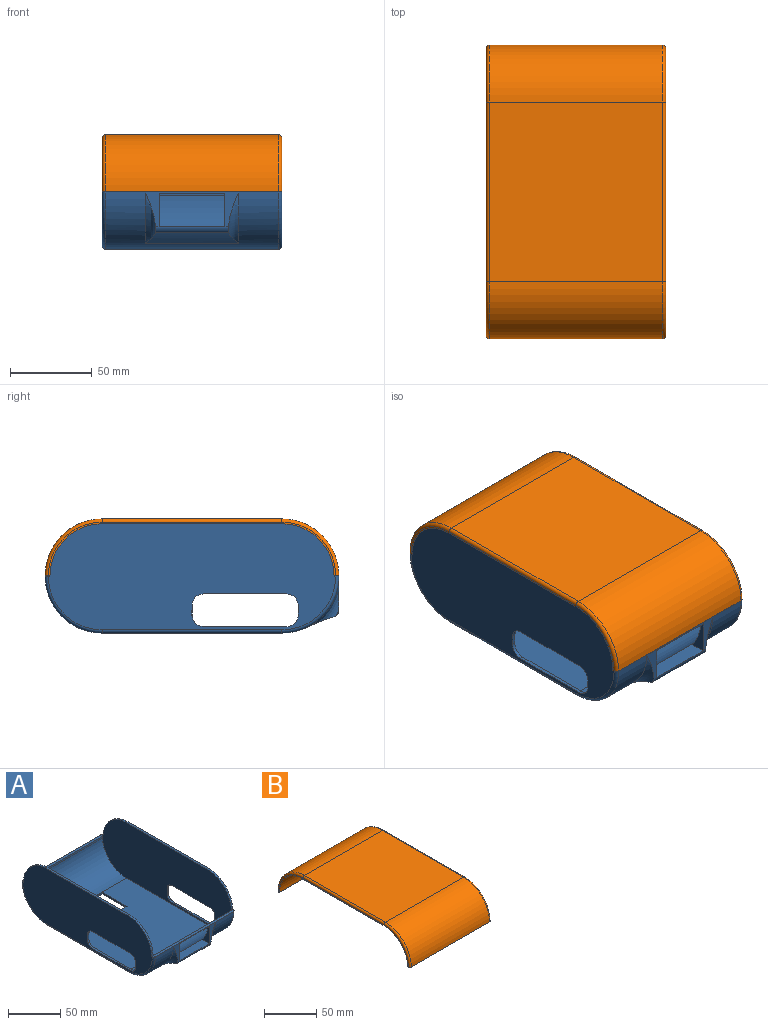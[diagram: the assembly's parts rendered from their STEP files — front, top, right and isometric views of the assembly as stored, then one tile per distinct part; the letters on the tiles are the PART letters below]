
ASSEMBLY  parts=2 mates=1
PART A: 307 faces, bbox 110x196.9x76 mm
  f0: plane 110x106mm, normal (0,0,-1), area 9197.1mm2, adj f6,f7,f38,f39,f40,f41,f42,f43
  f1: plane 110x106mm, normal (0,0,1), area 10332mm2, adj f17,f18,f20,f21,f38,f39,f40,f41
  f2: cylinder r=32mm len=32mm, axis (-1,0,0), area 100.5mm2, adj f4,f8,f13,f21
  f3: cylinder r=32mm len=32mm, axis (-1,0,0), area 100.5mm2, adj f4,f5,f13,f21
  f4: plane 110x2mm, normal (0,0,1), area 220mm2, adj f2,f3,f13,f21
  f5: plane 110x3mm, normal (0,0,1), area 328.3mm2, adj f3,f6,f11,f12,f13,f15,f291,f301
  f6: cylinder r=35mm len=106mm, axis (-1,0,0), area 3603.4mm2, adj f0,f5,f298,f299,f300,f301,f304
  f7: cylinder r=35mm len=106mm, axis (-1,0,0), area 5827.7mm2, adj f0,f8,f303,f306
  f8: plane 110x3mm, normal (0,0,1), area 328.3mm2, adj f2,f7,f9,f12,f13,f14,f303,f306
  f9: cylinder r=32mm len=32mm, axis (-1,0,0), area 100.5mm2, adj f8,f10,f12,f20
  f10: plane 110x2mm, normal (0,0,1), area 220mm2, adj f9,f11,f12,f20
  f11: cylinder r=32mm len=32mm, axis (-1,0,0), area 100.5mm2, adj f5,f10,f12,f20
  f12: plane 176x65mm, normal (1,0,0), area 9211.2mm2, adj f5,f8,f9,f10,f11,f22,f23,f24
  f13: plane 176x65mm, normal (-1,0,0), area 9211.2mm2, adj f2,f3,f4,f5,f8,f30,f31,f32
  f14: cylinder r=32mm len=106mm, axis (-1,0,0), area 212.1mm2, adj f8,f19,f20,f21
  f15: cylinder r=32mm len=106mm, axis (-1,0,0), area 212.1mm2, adj f5,f16,f20,f21
  f16: plane 106x1mm, normal (0,0,-1), area 106.2mm2, adj f15,f17,f20,f21,f292
  f17: cylinder r=33mm len=106mm, axis (-1,0,0), area 4437.5mm2, adj f1,f16,f20,f21,f294,f295,f296
  f18: cylinder r=33mm len=106mm, axis (-1,0,0), area 5282.5mm2, adj f1,f19,f20,f21
  f19: plane 106x1mm, normal (0,0,-1), area 106.2mm2, adj f14,f18,f20,f21
  f20: plane 175.88x65mm, normal (-1,0,0), area 9207.2mm2, adj f1,f9,f10,f11,f14,f15,f16,f17
  f21: plane 175.88x65mm, normal (1,0,0), area 9207.2mm2, adj f1,f2,f3,f4,f14,f15,f16,f17
  f22: plane 51x2mm, normal (0,0,-1), area 102mm2, adj f12,f20,f23,f29
  f23: cylinder r=7mm len=7mm, axis (1,0,0), area 22mm2, adj f12,f20,f22,f24
  f24: plane 6x2mm, normal (0,1,0), area 12mm2, adj f12,f20,f23,f25
  f25: cylinder r=7mm len=7mm, axis (1,0,0), area 22mm2, adj f12,f20,f24,f26
  f26: plane 51x2mm, normal (0,0,1), area 102mm2, adj f12,f20,f25,f27
  f27: cylinder r=7mm len=7mm, axis (1,0,0), area 22mm2, adj f12,f20,f26,f28
  f28: plane 6x2mm, normal (0,-1,0), area 12mm2, adj f12,f20,f27,f29
  f29: cylinder r=7mm len=7mm, axis (1,0,0), area 22mm2, adj f12,f20,f22,f28
  f30: plane 51x2mm, normal (0,0,-1), area 102mm2, adj f13,f21,f31,f37
  f31: cylinder r=7mm len=7mm, axis (-1,0,0), area 22mm2, adj f13,f21,f30,f32
  f32: plane 6x2mm, normal (0,-1,0), area 12mm2, adj f13,f21,f31,f33
  f33: cylinder r=7mm len=7mm, axis (-1,0,0), area 22mm2, adj f13,f21,f32,f34
  f34: plane 51x2mm, normal (0,0,1), area 102mm2, adj f13,f21,f33,f35
  f35: cylinder r=7mm len=7mm, axis (-1,0,0), area 22mm2, adj f13,f21,f34,f36
  f36: plane 6x2mm, normal (0,1,0), area 12mm2, adj f13,f21,f35,f37
  f37: cylinder r=7mm len=7mm, axis (-1,0,0), area 22mm2, adj f13,f21,f30,f36
  f38: plane 33.2x2mm, normal (-1,0,0), area 66.4mm2, adj f0,f1,f39,f41
  f39: plane 40x2mm, normal (0,1,0), area 80mm2, adj f0,f1,f38,f40
  f40: plane 33.2x2mm, normal (1,0,0), area 66.4mm2, adj f0,f1,f39,f41
  f41: plane 40x2mm, normal (0,-1,0), area 80mm2, adj f0,f1,f38,f40
  f42: plane 8.1x4.32mm, normal (0.88,0.47,0), area 9.2mm2, adj f0,f43,f50,f51
  f43: plane 8.1x4.29mm, normal (-0.88,0.47,0), area 9.2mm2, adj f0,f42,f44,f51
  f44: plane 2.06x1mm, normal (0,1,0), area 2.1mm2, adj f0,f43,f45,f51
  f45: plane 10.01x5.4mm, normal (0.88,-0.47,0), area 11.4mm2, adj f0,f44,f46,f51
  f46: plane 6.19x1mm, normal (1,0,0), area 6.2mm2, adj f0,f45,f47,f51
  f47: plane 1.9x1mm, normal (0,-1,0), area 1.9mm2, adj f0,f46,f48,f51
  f48: plane 6.28x1mm, normal (-1,0,0), area 6.3mm2, adj f0,f47,f49,f51
  f49: plane 9.92x5.41mm, normal (-0.88,-0.48,0), area 11.3mm2, adj f0,f48,f50,f51
  f50: plane 2.04x1mm, normal (0,1,0), area 2mm2, adj f0,f42,f49,f51
  f51: plane 16.2x12.71mm, normal (0,0,-1), area 49.8mm2, adj f42,f43,f44,f45,f46,f47,f48,f49
  f52: extruded ~1x0.94mm, area 0.9mm2, adj f0,f53,f70,f71
  f53: extruded ~1.43x1mm, area 1.6mm2, adj f0,f52,f54,f71
  f54: extruded ~1.68x1mm, area 1.8mm2, adj f0,f53,f55,f71
  f55: plane 7.15x1mm, normal (-1,0,0), area 7.1mm2, adj f0,f54,f56,f71
  f56: plane 3.52x1mm, normal (0,-1,0), area 3.5mm2, adj f0,f55,f57,f71
  f57: plane 1.43x1mm, normal (-1,0,0), area 1.4mm2, adj f0,f56,f58,f71
  f58: plane 3.52x1mm, normal (0,1,0), area 3.5mm2, adj f0,f57,f59,f71
  f59: plane 2.82x1mm, normal (-1,0,0), area 2.8mm2, adj f0,f58,f60,f71
  f60: plane 1.06x1mm, normal (0,1,0), area 1.1mm2, adj f0,f59,f61,f71
  f61: plane 2.59x1mm, normal (0.96,0.29,0), area 2.7mm2, adj f0,f60,f62,f71
  f62: plane 1.74x1mm, normal (0.4,0.92,0), area 1.9mm2, adj f0,f61,f63,f71
  f63: plane 1x0.89mm, normal (1,0,0), area 0.9mm2, adj f0,f62,f64,f71
  f64: plane 1.74x1mm, normal (0,-1,0), area 1.7mm2, adj f0,f63,f65,f71
  f65: plane 7.23x1mm, normal (1,0,0), area 7.2mm2, adj f0,f64,f66,f71
  f66: extruded ~3.71x3.52mm, area 5.9mm2, adj f0,f65,f67,f71
  f67: extruded ~1.05x1mm, area 1.1mm2, adj f0,f66,f68,f71
  f68: extruded ~1x0.88mm, area 0.9mm2, adj f0,f67,f69,f71
  f69: plane 1.41x1mm, normal (-1,0,0), area 1.4mm2, adj f0,f68,f70,f71
  f70: extruded ~1x0.72mm, area 0.7mm2, adj f0,f52,f69,f71
  f71: plane 15.18x7.19mm, normal (0,0,-1), area 38.2mm2, adj f52,f53,f54,f55,f56,f57,f58,f59
  f72: extruded ~1.13x1mm, area 1.2mm2, adj f0,f73,f79,f80
  f73: extruded ~1.15x1mm, area 1.2mm2, adj f0,f72,f74,f80
  f74: extruded ~1x0.94mm, area 1mm2, adj f0,f73,f75,f80
  f75: extruded ~1x1mm, area 1.1mm2, adj f0,f74,f76,f80
  f76: extruded ~1.11x1mm, area 1.2mm2, adj f0,f75,f77,f80
  f77: extruded ~1.13x1mm, area 1.2mm2, adj f0,f76,f78,f80
  f78: extruded ~1x1mm, area 1.1mm2, adj f0,f77,f79,f80
  f79: extruded ~1x0.97mm, area 1.1mm2, adj f0,f72,f78,f80
  f80: plane 3x2.67mm, normal (0,0,-1), area 6.6mm2, adj f72,f73,f74,f75,f76,f77,f78,f79
  f81: extruded ~4.99x1.4mm, area 5.3mm2, adj f82,f96,f97,f284
  f82: extruded ~4.95x1.4mm, area 5.2mm2, adj f81,f83,f97,f284
  f83: extruded ~4.09x1.7mm, area 4.6mm2, adj f82,f84,f97,f284
  f84: extruded ~4.05x1.69mm, area 4.5mm2, adj f83,f85,f97,f284
  f85: extruded ~4.96x1.37mm, area 5.2mm2, adj f84,f86,f97,f284
  f86: extruded ~5x1.37mm, area 5.3mm2, adj f85,f87,f97,f284
  f87: extruded ~4.07x1.69mm, area 4.6mm2, adj f86,f96,f97,f284
  f88: extruded ~6.12x1.97mm, area 6.6mm2, adj f0,f89,f95,f97
  f89: extruded ~6.12x1.96mm, area 6.6mm2, adj f0,f88,f90,f97
  f90: extruded ~5.45x2.22mm, area 6.1mm2, adj f0,f89,f91,f97
  f91: extruded ~5.54x2.18mm, area 6.1mm2, adj f0,f90,f92,f97
  f92: extruded ~6.13x1.95mm, area 6.6mm2, adj f0,f91,f93,f97
  f93: extruded ~6.18x1.94mm, area 6.6mm2, adj f0,f92,f94,f97
  f94: extruded ~5.52x2.19mm, area 6.1mm2, adj f0,f93,f95,f97
  f95: extruded ~5.47x2.23mm, area 6.1mm2, adj f0,f88,f94,f97
  f96: extruded ~4.07x1.7mm, area 4.6mm2, adj f81,f87,f97,f284
  f97: plane 16.68x14.9mm, normal (0,0,-1), area 83mm2, adj f81,f82,f83,f84,f85,f86,f87,f88
  f98: extruded ~3.55x1mm, area 3.7mm2, adj f99,f114,f115,f285
  f99: extruded ~3.53x1mm, area 3.7mm2, adj f98,f100,f115,f285
  f100: extruded ~2.72x1.19mm, area 3.1mm2, adj f99,f101,f115,f285
  f101: extruded ~2.77x1.2mm, area 3.1mm2, adj f100,f102,f115,f285
  f102: extruded ~3.52x1mm, area 3.7mm2, adj f101,f103,f115,f285
  f103: extruded ~3.55x1mm, area 3.7mm2, adj f102,f104,f115,f285
  f104: extruded ~2.74x1.21mm, area 3.1mm2, adj f103,f114,f115,f285
  f105: extruded ~4.64x1.49mm, area 5mm2, adj f0,f106,f113,f115
  f106: extruded ~4.59x1.5mm, area 4.9mm2, adj f0,f105,f107,f115
  f107: extruded ~4.05x1.7mm, area 4.5mm2, adj f0,f106,f108,f115
  f108: extruded ~4.12x1.66mm, area 4.6mm2, adj f0,f107,f109,f115
  f109: extruded ~4.63x1.49mm, area 5mm2, adj f0,f108,f110,f115
  f110: extruded ~3.35x1mm, area 3.4mm2, adj f0,f109,f111,f115
  f111: extruded ~2.19x1.95mm, area 3mm2, adj f0,f110,f112,f115
  f112: extruded ~2.89x1mm, area 3mm2, adj f0,f111,f113,f115
  f113: extruded ~4.13x1.67mm, area 4.6mm2, adj f0,f105,f112,f115
  f114: extruded ~2.74x1.22mm, area 3.1mm2, adj f98,f104,f115,f285
  f115: plane 12.59x11.16mm, normal (0,0,-1), area 56.6mm2, adj f98,f99,f100,f101,f102,f103,f104,f105
  f116: plane 5.39x1mm, normal (1,0,0), area 5.4mm2, adj f117,f132,f133,f286
  f117: plane 6.04x1mm, normal (0,1,0), area 6mm2, adj f116,f118,f133,f286
  f118: plane 7.2x5.06mm, normal (-0.82,-0.58,0), area 8.8mm2, adj f117,f119,f133,f286
  f119: extruded ~1.76x1mm, area 2mm2, adj f118,f120,f133,f286
  f120: plane 1x0.09mm, normal (0,-1,0), area 0.1mm2, adj f119,f132,f133,f286
  f121: plane 2.4x1mm, normal (0,-1,0), area 2.4mm2, adj f0,f122,f131,f133
  f122: plane 1.67x1mm, normal (-1,0,0), area 1.7mm2, adj f0,f121,f123,f133
  f123: plane 2.4x1mm, normal (0,1,0), area 2.4mm2, adj f0,f122,f124,f133
  f124: plane 10.89x1mm, normal (-1,0,0), area 10.9mm2, adj f0,f123,f125,f133
  f125: plane 1.95x1mm, normal (0,1,0), area 2mm2, adj f0,f124,f126,f133
  f126: plane 10.96x7.69mm, normal (0.82,0.57,0), area 13.4mm2, adj f0,f125,f127,f133
  f127: plane 1.61x1mm, normal (1,0,0), area 1.6mm2, adj f0,f126,f128,f133
  f128: plane 7.88x1mm, normal (0,-1,0), area 7.9mm2, adj f0,f127,f129,f133
  f129: plane 3.72x1mm, normal (1,0,0), area 3.7mm2, adj f0,f128,f130,f133
  f130: plane 1.76x1mm, normal (0,-1,0), area 1.8mm2, adj f0,f129,f131,f133
  f131: plane 3.72x1mm, normal (-1,0,0), area 3.7mm2, adj f0,f121,f130,f133
  f132: extruded ~3.58x1mm, area 3.6mm2, adj f116,f120,f133,f286
  f133: plane 16.29x12.04mm, normal (0,0,-1), area 63.4mm2, adj f116,f117,f118,f119,f120,f121,f122,f123
  f134: extruded ~5.15x1mm, area 5.3mm2, adj f135,f149,f150,f287
  f135: extruded ~5.14x1mm, area 5.2mm2, adj f134,f136,f150,f287
  f136: extruded ~2.65x1.6mm, area 3.3mm2, adj f135,f137,f150,f287
  f137: extruded ~2.66x1.62mm, area 3.3mm2, adj f136,f138,f150,f287
  f138: extruded ~5.11x1mm, area 5.2mm2, adj f137,f139,f150,f287
  f139: extruded ~5.13x1mm, area 5.2mm2, adj f138,f140,f150,f287
  f140: extruded ~2.66x1.63mm, area 3.3mm2, adj f139,f149,f150,f287
  f141: extruded ~6.27x1.32mm, area 6.5mm2, adj f0,f142,f148,f150
  f142: extruded ~6.19x1.37mm, area 6.4mm2, adj f0,f141,f143,f150
  f143: extruded ~4.01x2.14mm, area 4.8mm2, adj f0,f142,f144,f150
  f144: extruded ~4.02x2.05mm, area 4.7mm2, adj f0,f143,f145,f150
  f145: extruded ~6.28x1.32mm, area 6.5mm2, adj f0,f144,f146,f150
  f146: extruded ~6.22x1.36mm, area 6.5mm2, adj f0,f145,f147,f150
  f147: extruded ~3.98x2.12mm, area 4.7mm2, adj f0,f146,f148,f150
  f148: extruded ~4.05x2.07mm, area 4.8mm2, adj f0,f141,f147,f150
  f149: extruded ~2.65x1.61mm, area 3.3mm2, adj f134,f140,f150,f287
  f150: plane 16.68x10.71mm, normal (0,0,-1), area 69.3mm2, adj f134,f135,f136,f137,f138,f139,f140,f141
  f151: plane 6.06x1mm, normal (-1,0,0), area 6.1mm2, adj f152,f175,f176,f288
  f152: plane 3.23x1mm, normal (0,-1,0), area 3.2mm2, adj f151,f153,f176,f288
  f153: extruded ~3.08x1mm, area 3.2mm2, adj f152,f154,f176,f288
  f154: extruded ~2.22x1.01mm, area 2.5mm2, adj f153,f155,f176,f288
  f155: extruded ~2.38x1mm, area 2.7mm2, adj f154,f156,f176,f288
  f156: extruded ~2.95x1mm, area 3.1mm2, adj f155,f175,f176,f288
  f157: plane 3.1x1mm, normal (0,1,0), area 3.1mm2, adj f158,f173,f176,f177
  f158: plane 5.3x1mm, normal (-1,0,0), area 5.3mm2, adj f157,f159,f176,f177
  f159: plane 2.77x1mm, normal (0,-1,0), area 2.8mm2, adj f158,f160,f176,f177
  f160: extruded ~3.1x1mm, area 3.2mm2, adj f159,f161,f176,f177
  f161: extruded ~1.97x1mm, area 2.3mm2, adj f160,f162,f176,f177
  f162: extruded ~2.11x1mm, area 2.4mm2, adj f161,f173,f176,f177
  f163: plane 4.58x1mm, normal (0,1,0), area 4.6mm2, adj f0,f164,f174,f176
  f164: plane 16.2x1mm, normal (1,0,0), area 16.2mm2, adj f0,f163,f165,f176
  f165: plane 5.65x1mm, normal (0,-1,0), area 5.7mm2, adj f0,f164,f166,f176
  f166: extruded ~4.11x1.22mm, area 4.4mm2, adj f0,f165,f167,f176
  f167: extruded ~3.39x1.47mm, area 3.8mm2, adj f0,f166,f168,f176
  f168: extruded ~3.88x3.69mm, area 5.9mm2, adj f0,f167,f169,f176
  f169: plane 1x0.11mm, normal (-1,0,0), area 0.1mm2, adj f0,f168,f170,f176
  f170: extruded ~2.35x1.21mm, area 2.7mm2, adj f0,f169,f171,f176
  f171: extruded ~2.38x1mm, area 2.6mm2, adj f0,f170,f172,f176
  f172: extruded ~3.05x1.44mm, area 3.5mm2, adj f0,f171,f174,f176
  f173: extruded ~2.87x1mm, area 3mm2, adj f157,f162,f176,f177
  f174: extruded ~4.66x1mm, area 4.8mm2, adj f0,f163,f172,f176
  f175: plane 3.38x1mm, normal (0,1,0), area 3.4mm2, adj f151,f156,f176,f288
  f176: plane 16.2x11.23mm, normal (0,0,-1), area 89.5mm2, adj f151,f152,f153,f154,f155,f156,f157,f158
  f177: plane 6.85x5.3mm, normal (0,0,-1), area 33.2mm2, adj f157,f158,f159,f160,f161,f162,f173
  f178: extruded ~5.5x1mm, area 5.6mm2, adj f0,f179,f187,f188
  f179: extruded ~5.41x1mm, area 5.5mm2, adj f0,f178,f180,f188
  f180: extruded ~4.4x2.48mm, area 5.1mm2, adj f0,f179,f181,f188
  f181: plane 1.77x1mm, normal (0,-1,0), area 1.8mm2, adj f0,f180,f182,f188
  f182: extruded ~4.63x2.36mm, area 5.2mm2, adj f0,f181,f183,f188
  f183: extruded ~5.2x1mm, area 5.3mm2, adj f0,f182,f184,f188
  f184: extruded ~5.27x1mm, area 5.3mm2, adj f0,f183,f185,f188
  f185: extruded ~4.7x2.4mm, area 5.3mm2, adj f0,f184,f186,f188
  f186: plane 1.79x1mm, normal (0,1,0), area 1.8mm2, adj f0,f185,f187,f188
  f187: extruded ~4.49x2.48mm, area 5.2mm2, adj f0,f178,f186,f188
  f188: plane 19.79x5.13mm, normal (0,0,-1), area 38.1mm2, adj f178,f179,f180,f181,f182,f183,f184,f185
  f189: plane 10.48x1mm, normal (-1,0,0), area 10.5mm2, adj f0,f190,f202,f203
  f190: plane 1.88x1mm, normal (0,1,0), area 1.9mm2, adj f0,f189,f191,f203
  f191: plane 10.55x1mm, normal (1,0,0), area 10.5mm2, adj f0,f190,f192,f203
  f192: extruded ~3.13x1.11mm, area 3.4mm2, adj f0,f191,f193,f203
  f193: extruded ~3.16x1.09mm, area 3.4mm2, adj f0,f192,f194,f203
  f194: extruded ~3.26x1.09mm, area 3.5mm2, adj f0,f193,f195,f203
  f195: extruded ~3.11x1.11mm, area 3.4mm2, adj f0,f194,f196,f203
  f196: plane 10.57x1mm, normal (-1,0,0), area 10.6mm2, adj f0,f195,f197,f203
  f197: plane 1.89x1mm, normal (0,1,0), area 1.9mm2, adj f0,f196,f198,f203
  f198: plane 10.44x1mm, normal (1,0,0), area 10.4mm2, adj f0,f197,f199,f203
  f199: extruded ~4.39x1.6mm, area 4.8mm2, adj f0,f198,f200,f203
  f200: extruded ~4.53x1.6mm, area 4.9mm2, adj f0,f199,f201,f203
  f201: extruded ~4.6x1.59mm, area 5mm2, adj f0,f200,f202,f203
  f202: extruded ~4.36x1.67mm, area 4.8mm2, adj f0,f189,f201,f203
  f203: plane 16.42x12.4mm, normal (0,0,-1), area 69mm2, adj f189,f190,f191,f192,f193,f194,f195,f196
  f204: plane 7.86x1mm, normal (1,0,0), area 7.9mm2, adj f0,f205,f220,f221
  f205: plane 1.84x1mm, normal (0,-1,0), area 1.8mm2, adj f0,f204,f206,f221
  f206: plane 7.92x1mm, normal (-1,0,0), area 7.9mm2, adj f0,f205,f207,f221
  f207: extruded ~3.39x1.11mm, area 3.7mm2, adj f0,f206,f208,f221
  f208: extruded ~3.3x1.06mm, area 3.6mm2, adj f0,f207,f209,f221
  f209: extruded ~2.27x1mm, area 2.3mm2, adj f0,f208,f210,f221
  f210: extruded ~1.59x1.39mm, area 2.1mm2, adj f0,f209,f211,f221
  f211: plane 1x0.09mm, normal (0,1,0), area 0.1mm2, adj f0,f210,f212,f221
  f212: plane 1.66x1mm, normal (-0.98,0.18,0), area 1.7mm2, adj f0,f211,f213,f221
  f213: plane 1.5x1mm, normal (0,1,0), area 1.5mm2, adj f0,f212,f214,f221
  f214: plane 12.14x1mm, normal (1,0,0), area 12.1mm2, adj f0,f213,f215,f221
  f215: plane 1.84x1mm, normal (0,-1,0), area 1.8mm2, adj f0,f214,f216,f221
  f216: plane 6.37x1mm, normal (-1,0,0), area 6.4mm2, adj f0,f215,f217,f221
  f217: extruded ~3.4x1mm, area 3.6mm2, adj f0,f216,f218,f221
  f218: extruded ~2.79x1.03mm, area 3.1mm2, adj f0,f217,f219,f221
  f219: extruded ~2.12x1mm, area 2.3mm2, adj f0,f218,f220,f221
  f220: extruded ~2.21x1mm, area 2.4mm2, adj f0,f204,f219,f221
  f221: plane 12.37x10.15mm, normal (0,0,-1), area 53.5mm2, adj f204,f205,f206,f207,f208,f209,f210,f211
  f222: plane 1.84x1mm, normal (0,-1,0), area 1.8mm2, adj f0,f223,f225,f226
  f223: plane 12.14x1mm, normal (-1,0,0), area 12.1mm2, adj f0,f222,f224,f226
  f224: plane 1.84x1mm, normal (0,1,0), area 1.8mm2, adj f0,f223,f225,f226
  f225: plane 12.14x1mm, normal (1,0,0), area 12.1mm2, adj f0,f222,f224,f226
  f226: plane 12.14x1.84mm, normal (0,0,-1), area 22.3mm2, adj f222,f223,f224,f225
  f227: extruded ~1x0.93mm, area 1mm2, adj f0,f228,f234,f235
  f228: extruded ~1x0.93mm, area 1mm2, adj f0,f227,f229,f235
  f229: extruded ~1x0.78mm, area 0.9mm2, adj f0,f228,f230,f235
  f230: extruded ~1x0.76mm, area 0.8mm2, adj f0,f229,f231,f235
  f231: extruded ~1x0.93mm, area 1mm2, adj f0,f230,f232,f235
  f232: extruded ~1x0.92mm, area 1mm2, adj f0,f231,f233,f235
  f233: extruded ~1x0.76mm, area 0.8mm2, adj f0,f232,f234,f235
  f234: extruded ~1x0.78mm, area 0.9mm2, adj f0,f227,f233,f235
  f235: plane 2.45x2.17mm, normal (0,0,-1), area 4.3mm2, adj f227,f228,f229,f230,f231,f232,f233,f234
  f236: extruded ~1x0.94mm, area 0.9mm2, adj f0,f237,f254,f255
  f237: extruded ~1.43x1mm, area 1.6mm2, adj f0,f236,f238,f255
  f238: extruded ~1.68x1mm, area 1.8mm2, adj f0,f237,f239,f255
  f239: plane 7.15x1mm, normal (-1,0,0), area 7.1mm2, adj f0,f238,f240,f255
  f240: plane 3.52x1mm, normal (0,-1,0), area 3.5mm2, adj f0,f239,f241,f255
  f241: plane 1.43x1mm, normal (-1,0,0), area 1.4mm2, adj f0,f240,f242,f255
  f242: plane 3.52x1mm, normal (0,1,0), area 3.5mm2, adj f0,f241,f243,f255
  f243: plane 2.82x1mm, normal (-1,0,0), area 2.8mm2, adj f0,f242,f244,f255
  f244: plane 1.06x1mm, normal (0,1,0), area 1.1mm2, adj f0,f243,f245,f255
  f245: plane 2.59x1mm, normal (0.96,0.29,0), area 2.7mm2, adj f0,f244,f246,f255
  f246: plane 1.74x1mm, normal (0.4,0.92,0), area 1.9mm2, adj f0,f245,f247,f255
  f247: plane 1x0.89mm, normal (1,0,0), area 0.9mm2, adj f0,f246,f248,f255
  f248: plane 1.74x1mm, normal (0,-1,0), area 1.7mm2, adj f0,f247,f249,f255
  f249: plane 7.23x1mm, normal (1,0,0), area 7.2mm2, adj f0,f248,f250,f255
  f250: extruded ~3.71x3.52mm, area 5.9mm2, adj f0,f249,f251,f255
  f251: extruded ~1.05x1mm, area 1.1mm2, adj f0,f250,f252,f255
  f252: extruded ~1x0.88mm, area 0.9mm2, adj f0,f251,f253,f255
  f253: plane 1.41x1mm, normal (-1,0,0), area 1.4mm2, adj f0,f252,f254,f255
  f254: extruded ~1x0.72mm, area 0.7mm2, adj f0,f236,f253,f255
  f255: plane 15.18x7.19mm, normal (0,0,-1), area 38.2mm2, adj f236,f237,f238,f239,f240,f241,f242,f243
  f256: plane 1.98x1mm, normal (0,1,0), area 2mm2, adj f0,f257,f271,f272
  f257: plane 12.21x4.9mm, normal (0.93,-0.37,0), area 13.2mm2, adj f0,f256,f258,f272
  f258: plane 1.73x1mm, normal (0.93,0.37,0), area 1.9mm2, adj f0,f257,f259,f272
  f259: extruded ~2.71x2.13mm, area 3.7mm2, adj f0,f258,f260,f272
  f260: extruded ~1.36x1mm, area 1.4mm2, adj f0,f259,f261,f272
  f261: plane 1.47x1mm, normal (1,0,0), area 1.5mm2, adj f0,f260,f262,f272
  f262: extruded ~1.66x1mm, area 1.7mm2, adj f0,f261,f263,f272
  f263: extruded ~2.54x1mm, area 2.7mm2, adj f0,f262,f264,f272
  f264: extruded ~2.91x1.81mm, area 3.5mm2, adj f0,f263,f265,f272
  f265: plane 13.83x5.22mm, normal (-0.94,-0.35,0), area 14.8mm2, adj f0,f264,f266,f272
  f266: plane 1.97x1mm, normal (0,1,0), area 2mm2, adj f0,f265,f267,f272
  f267: extruded ~8.41x3.01mm, area 8.9mm2, adj f0,f266,f268,f272
  f268: extruded ~1.94x1mm, area 2mm2, adj f0,f267,f269,f272
  f269: plane 1x0.09mm, normal (0,1,0), area 0.1mm2, adj f0,f268,f270,f272
  f270: extruded ~3.43x1.09mm, area 3.6mm2, adj f0,f269,f271,f272
  f271: plane 6.92x2.66mm, normal (-0.93,0.36,0), area 7.4mm2, adj f0,f256,f270,f272
  f272: plane 17.6x11.39mm, normal (0,0,-1), area 57.2mm2, adj f256,f257,f258,f259,f260,f261,f262,f263
  f273: extruded ~5.43x1mm, area 5.5mm2, adj f0,f274,f282,f283
  f274: extruded ~5.48x1mm, area 5.6mm2, adj f0,f273,f275,f283
  f275: extruded ~4.5x2.48mm, area 5.2mm2, adj f0,f274,f276,f283
  f276: plane 1.79x1mm, normal (0,1,0), area 1.8mm2, adj f0,f275,f277,f283
  f277: extruded ~4.7x2.4mm, area 5.3mm2, adj f0,f276,f278,f283
  f278: extruded ~5.27x1mm, area 5.3mm2, adj f0,f277,f279,f283
  f279: extruded ~5.2x1mm, area 5.3mm2, adj f0,f278,f280,f283
  f280: extruded ~4.63x2.36mm, area 5.2mm2, adj f0,f279,f281,f283
  f281: plane 1.77x1mm, normal (0,-1,0), area 1.8mm2, adj f0,f280,f282,f283
  f282: extruded ~4.38x2.48mm, area 5.1mm2, adj f0,f273,f281,f283
  f283: plane 19.79x5.13mm, normal (0,0,-1), area 38.1mm2, adj f273,f274,f275,f276,f277,f278,f279,f280
  f284: plane 13.34x10.91mm, normal (0,0,-1), area 120.7mm2, adj f81,f82,f83,f84,f85,f86,f87,f96
  f285: plane 9.48x7.35mm, normal (0,0,-1), area 57.8mm2, adj f98,f99,f100,f101,f102,f103,f104,f114
  f286: plane 8.96x6.15mm, normal (0,0,-1), area 26.2mm2, adj f116,f117,f118,f119,f120,f132
  f287: plane 13.5x6.97mm, normal (0,0,-1), area 79.4mm2, adj f134,f135,f136,f137,f138,f139,f140,f149
  f288: plane 7.33x6.06mm, normal (0,0,-1), area 40.5mm2, adj f151,f152,f153,f154,f155,f156,f175
  f289: plane 3.44x2.35mm, normal (-1,0,0), area 1.5mm2, adj f297,f299
  f290: plane 3.44x2.35mm, normal (1,0,0), area 1.5mm2, adj f297,f298
  f291: plane 57x21.1mm, normal (0,-1,0), area 238.9mm2, adj f5,f293,f294,f295,f297,f298,f299
  f292: cylinder r=33mm len=40.2mm, axis (-1,0,0), area 40.2mm2, adj f16,f293,f294,f295
  f293: plane 40.2x2.02mm, normal (0,0,-1), area 81mm2, adj f291,f292,f294,f295
  f294: plane 20.2x9.71mm, normal (1,0,0), area 92.1mm2, adj f17,f291,f292,f293,f296,f297
  f295: plane 20.2x9.71mm, normal (-1,0,0), area 92.1mm2, adj f17,f291,f292,f293,f296,f297
  f296: plane 40.2x9.71mm, normal (0,0,1), area 390.3mm2, adj f17,f294,f295,f297
  f297: cylinder r=4.1mm len=45.02mm, axis (1,0,0), area 234.6mm2, adj f289,f290,f291,f294,f295,f296,f298,f299
  f298: torus R=41mm, axis (-1,0,0), area 192.3mm2, adj f6,f290,f291,f297,f300
  f299: torus R=41mm, axis (-1,0,0), area 192.3mm2, adj f6,f289,f291,f297,f300
  f300: cylinder r=100mm len=57mm, axis (-1,0,0), area 885.9mm2, adj f6,f297,f298,f299
  f301: torus R=33mm, axis (1,0,0), area 169.1mm2, adj f5,f6,f13,f302
  f302: cylinder r=2mm len=110mm, axis (0,1,0), area 345.6mm2, adj f0,f13,f301,f303
  f303: torus R=33mm, axis (1,0,0), area 169.1mm2, adj f7,f8,f13,f302
  f304: torus R=33mm, axis (1,0,0), area 169.1mm2, adj f5,f6,f12,f305
  f305: cylinder r=2mm len=110mm, axis (0,-1,0), area 345.6mm2, adj f0,f12,f304,f306
  f306: torus R=33mm, axis (1,0,0), area 169.1mm2, adj f7,f8,f12,f305
PART B: 16 faces, bbox 110x185.8x37.9 mm
  f0: cylinder r=35mm len=106mm, axis (-1,0,0), area 5827.7mm2, adj f1,f7,f12,f15
  f1: plane 110x106mm, normal (0,0,1), area 11660mm2, adj f0,f2,f11,f14
  f2: cylinder r=35mm len=106mm, axis (-1,0,0), area 5827.7mm2, adj f1,f3,f10,f13
  f3: plane 110x3mm, normal (0,0,-1), area 328.3mm2, adj f2,f4,f8,f9,f10,f13
  f4: cylinder r=32mm len=110mm, axis (-1,0,0), area 5529.2mm2, adj f3,f5,f8,f9
  f5: plane 110x110mm, normal (0,0,-1), area 12100mm2, adj f4,f6,f8,f9
  f6: cylinder r=32mm len=110mm, axis (-1,0,0), area 5529.2mm2, adj f5,f7,f8,f9
  f7: plane 110x3mm, normal (0,0,-1), area 328.3mm2, adj f0,f6,f8,f9,f12,f15
  f8: plane 176x33mm, normal (1,0,0), area 212.1mm2, adj f3,f4,f5,f6,f7,f13,f14,f15
  f9: plane 176x33mm, normal (-1,0,0), area 212.1mm2, adj f3,f4,f5,f6,f7,f10,f11,f12
  f10: torus R=33mm, axis (1,0,0), area 169.1mm2, adj f2,f3,f9,f11
  f11: cylinder r=2mm len=110mm, axis (0,-1,0), area 345.6mm2, adj f1,f9,f10,f12
  f12: torus R=33mm, axis (1,0,0), area 169.1mm2, adj f0,f7,f9,f11
  f13: torus R=33mm, axis (1,0,0), area 169.1mm2, adj f2,f3,f8,f14
  f14: cylinder r=2mm len=110mm, axis (0,1,0), area 345.6mm2, adj f1,f8,f13,f15
  f15: torus R=33mm, axis (1,0,0), area 169.1mm2, adj f0,f7,f8,f14
PLACE A t=(-0.14,0.24,-16.33)mm fixed
PLACE B t=(-0.14,0.24,-16.33)mm
MATE slider A.f5 <-> B.f3  axis (0,0,1) through (-0.14,-88.26,18.67)mm
